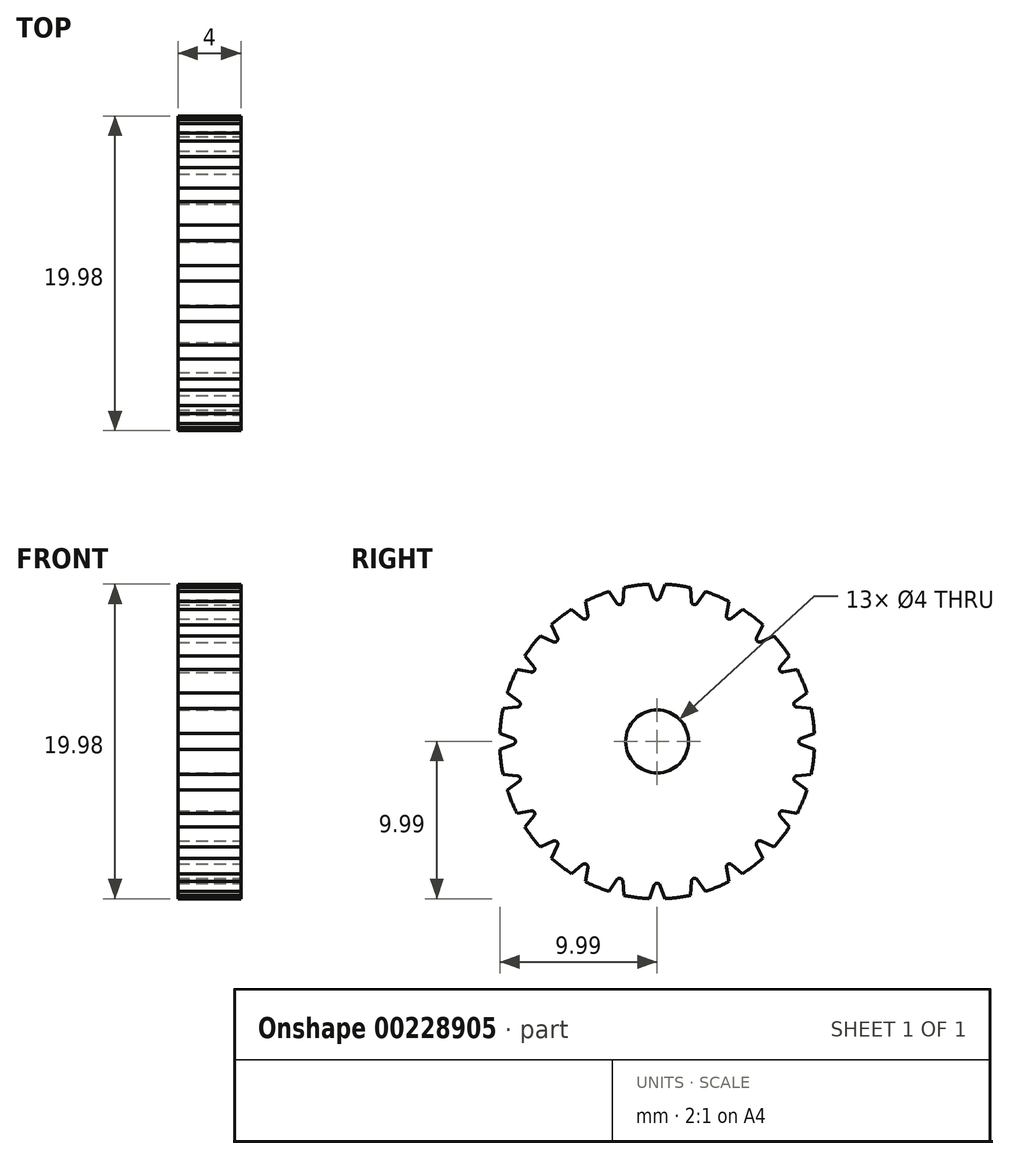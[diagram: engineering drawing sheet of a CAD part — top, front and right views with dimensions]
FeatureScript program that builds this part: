
annotation { "Feature Type Name" : "Feature", "Feature Type Description" : "" }
export const myFeature = defineFeature(function(context is Context, id is Id, definition is map)
    precondition{}
    {
        {
            var Q0;
            Q0=qCreatedBy(makeId("Front.planeOp"),FACE);
            var sketch = newSketch(context, id + "F0", { "sketchPlane" : qUnion([Q0])});
            skLineSegment(sketch, "E0", {"start": v(0, 0) * mm, "end": v(-2, 0) * mm, "construction": true});
            skLineSegment(sketch, "E1", {"start": v(0, 0) * mm, "end": v(0, 2) * mm, "construction": true});
            skLineSegment(sketch, "E2", {"start": v(0, 2) * mm, "end": v(-2, 2) * mm});
            skLineSegment(sketch, "E3", {"start": v(-2, 2) * mm, "end": v(-2, 10) * mm});
            skLineSegment(sketch, "E4", {"start": v(-2, 10) * mm, "end": v(0, 10) * mm});
            skLineSegment(sketch, "E5.MirrorCS", {"start": v(0, 2) * mm, "end": v(2, 2) * mm});
            skLineSegment(sketch, "E6.MirrorCS", {"start": v(2, 2) * mm, "end": v(2, 10) * mm});
            skLineSegment(sketch, "E7.MirrorCS", {"start": v(2, 10) * mm, "end": v(0, 10) * mm});
            skLineSegment(sketch, "E8", {"start": v(0, 2) * mm, "end": v(0, 10) * mm, "construction": true});
            skSolve(sketch);
        }
        {
            var Q0;
            Q0=makeQuery(id+"F0.imprint","IMPRINT",FACE,{"disambiguationData":[TD([[makeQuery(id+"F0.imprint","IMPRINT",EDGE,{"derivedFrom":sQuery(id+"F0.wireOp",EDGE,"E2")}),-1.0]])]});
            var Q1;
            Q1=sQuery(id+"F0.wireOp",EDGE,"E0");
            revolve(context, id + "F1", {"entities" : qUnion([Q0]), "axis" : qUnion([Q1]), "revolveType" : RevolveType.FULL});
        }
        {
            var Q0;
            Q0=qCreatedBy(makeId("Right.planeOp"),FACE);
            var sketch = newSketch(context, id + "F2", { "sketchPlane" : qUnion([Q0])});
            skArc(sketch, "E9", {"start": v(0, 9) * mm, "mid": v(0, 9) * mm, "end": v(0, 9) * mm});
            skLineSegment(sketch, "E10", {"start": v(0, 0) * mm, "end": v(0, 10) * mm, "construction": true});
            skLineSegment(sketch, "E11", {"start": v(0.19, 9.13) * mm, "end": v(0.74, 10.63) * mm});
            skLineSegment(sketch, "E12.MirrorCS", {"start": v(-0.19, 9.13) * mm, "end": v(-0.74, 10.63) * mm});
            skPoint(sketch, "E13.visualSharp", {"position": v(-0.14, 9) * mm});
            skArc(sketch, "E13.filletArc", {"start": v(-0.19, 9.13) * mm, "mid": v(-0.12, 9.04) * mm, "end": v(0, 9) * mm});
            skPoint(sketch, "E14.visualSharp", {"position": v(0.14, 9) * mm});
            skArc(sketch, "E14.filletArc", {"start": v(0, 9) * mm, "mid": v(0.12, 9.04) * mm, "end": v(0.19, 9.13) * mm});
            skPoint(sketch, "E15.orphan", {"position": v(-0.5, 9.99) * mm});
            skPoint(sketch, "E16.orphan", {"position": v(0.5, 9.99) * mm});
            skLineSegment(sketch, "E17", {"start": v(-0.74, 10.63) * mm, "end": v(0.74, 10.63) * mm});
            skSolve(sketch);
        }
        {
            var Q0;
            Q0 = qSketchRegion(id + "F2", true);
            extrude(context, id + "F3", {"entities" : qUnion([Q0]), "operationType" : NewBodyOperationType.REMOVE, "endBound" : BoundingType.SYMMETRIC, "oppositeDirection" : true, "depth" : 25 * mm});
        }
        {
            var Q0;
            Q0=makeQuery(id+"F3.boolean.opBoolean","COPY",FACE,{"derivedFrom":makeQuery(id+"F3.opExtrude","SWEPT_FACE",FACE,{"disambiguationData":[OSD([sQuery(id+"F2.wireOp",EDGE,"E12.MirrorCS")])]})});
            var Q1;
            Q1=makeQuery(id+"F3.boolean.opBoolean","COPY",FACE,{"derivedFrom":makeQuery(id+"F3.opExtrude","SWEPT_FACE",FACE,{"disambiguationData":[OSD([sQuery(id+"F2.wireOp",EDGE,"E13.filletArc")])]})});
            var Q2;
            Q2=makeQuery(id+"F3.boolean.opBoolean","COPY",FACE,{"derivedFrom":makeQuery(id+"F3.opExtrude","SWEPT_FACE",FACE,{"disambiguationData":[OSD([sQuery(id+"F2.wireOp",EDGE,"E9")])]})});
            var Q3;
            Q3=makeQuery(id+"F3.boolean.opBoolean","COPY",FACE,{"derivedFrom":makeQuery(id+"F3.opExtrude","SWEPT_FACE",FACE,{"disambiguationData":[OSD([sQuery(id+"F2.wireOp",EDGE,"E14.filletArc")])]})});
            var Q4;
            Q4=makeQuery(id+"F3.boolean.opBoolean","COPY",FACE,{"derivedFrom":makeQuery(id+"F3.opExtrude","SWEPT_FACE",FACE,{"disambiguationData":[OSD([sQuery(id+"F2.wireOp",EDGE,"E11")])]})});
            var Q5;
            Q5=makeQuery(id+"F1.opRevolve","SWEPT_FACE",FACE,{"disambiguationData":[OSD([sQuery(id+"F0.wireOp",EDGE,"E4"),sQuery(id+"F0.wireOp",EDGE,"E7.MirrorCS")])]});
            circularPattern(context, id + "F4", {"patternType" : PatternType.FACE, "faces" : qUnion([Q0, Q1, Q2, Q3, Q4]), "axis" : qUnion([Q5]), "angle" : 15 * degree, "instanceCount" : 24});
        }
    });
